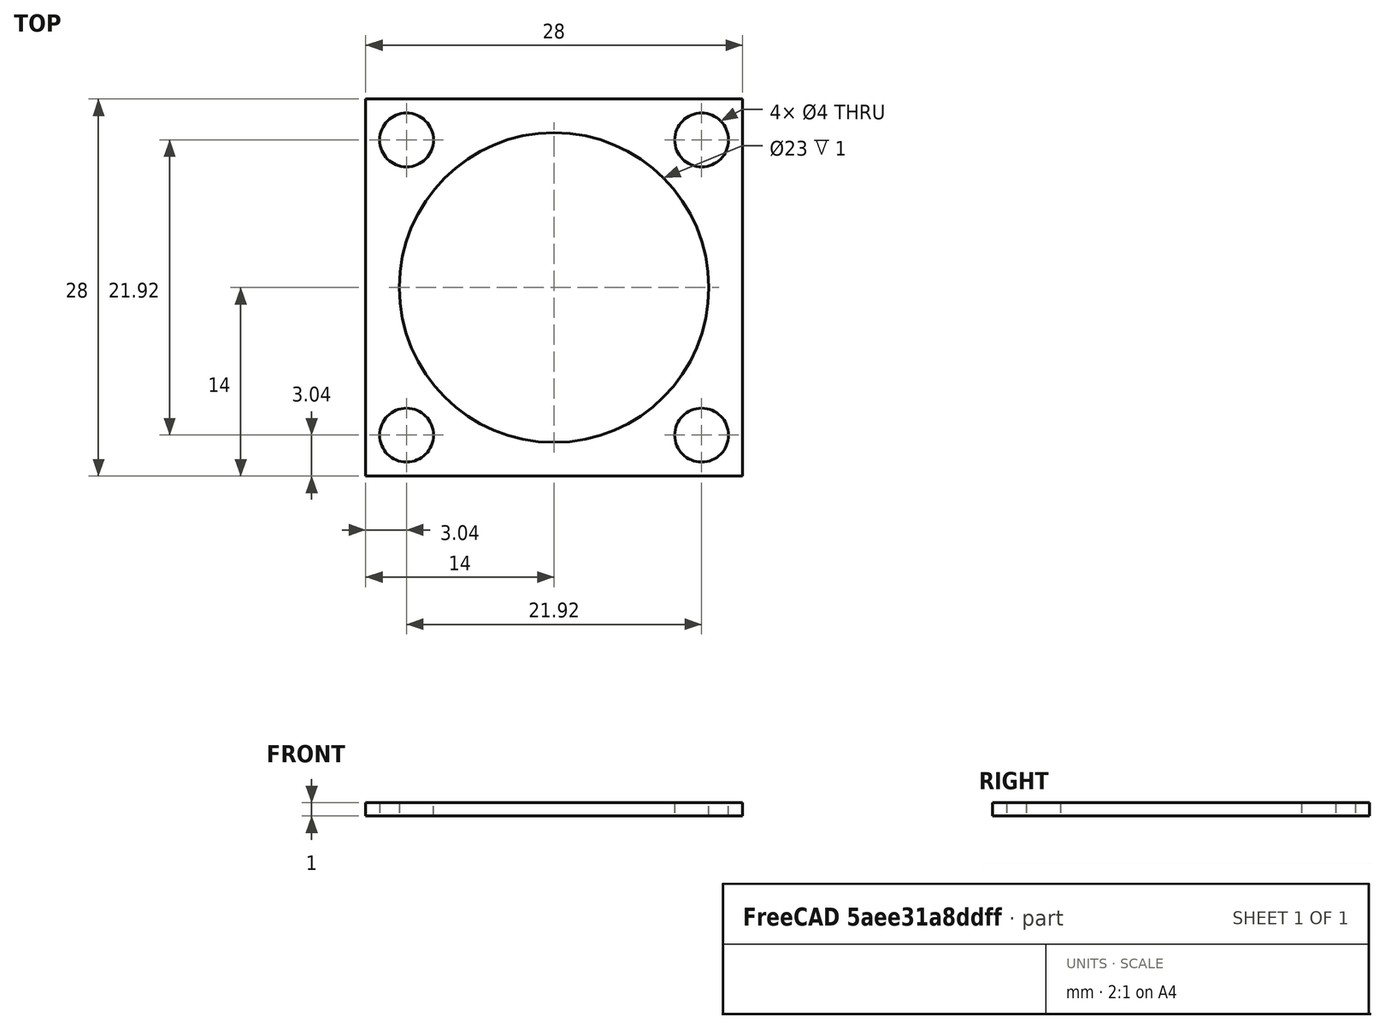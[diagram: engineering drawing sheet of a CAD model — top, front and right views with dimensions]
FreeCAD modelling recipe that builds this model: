
FCSTD DOCUMENT  (FreeCAD 0.19R24276 (Git))
Label: AS5048_holder_spacer
License: All rights reserved
LicenseURL: http://en.wikipedia.org/wiki/All_rights_reserved
objects: Sketcher::SketchObject×2, PartDesign::Body×2, PartDesign::Pad×1
note: 6 computed .brp shape members not serialized (recipe doc carries the construction recipe); baked Part::Feature solids carry a one-line shape summary decoded from their .brp

FEATURE [Sketcher::SketchObject] Sketch
  FullyConstrained = true
  MapMode = 5
  Support = -> [XY_Plane]
FEATURE [PartDesign::Body] Body
  Group = -> [Sketch]
  Origin = -> Origin
FEATURE [Sketcher::SketchObject] Sketch001
  FullyConstrained = false
  MapMode = 5
  Support = -> [XY_Plane001]
  sketch-geometry (9):
    g0: LineSegment StartX=-14 StartY=-14 StartZ=0 EndX=14 EndY=-14 EndZ=0
    g1: LineSegment StartX=14 StartY=-14 StartZ=0 EndX=14 EndY=14 EndZ=0
    g2: LineSegment StartX=14 StartY=14 StartZ=0 EndX=-14 EndY=14 EndZ=0
    g3: LineSegment StartX=-14 StartY=14 StartZ=0 EndX=-14 EndY=-14 EndZ=0
    g4: Circle CenterX=-10.9602 CenterY=10.9602 CenterZ=0 NormalX=0 NormalY=0 NormalZ=1 AngleXU=0 Radius=2
    g5: Circle CenterX=-10.9602 CenterY=-10.9602 CenterZ=0 NormalX=0 NormalY=0 NormalZ=1 AngleXU=0 Radius=2
    g6: Circle CenterX=10.9602 CenterY=10.9602 CenterZ=0 NormalX=0 NormalY=0 NormalZ=1 AngleXU=0 Radius=2
    g7: Circle CenterX=10.9602 CenterY=-10.9602 CenterZ=0 NormalX=0 NormalY=0 NormalZ=1 AngleXU=0 Radius=2
    g8: Circle CenterX=0 CenterY=0 CenterZ=0 NormalX=0 NormalY=0 NormalZ=1 AngleXU=0 Radius=11.5
  constraints (17):
    c: Coincident(g0,g1)
    c: Coincident(g1,g2)
    c: Coincident(g2,g3)
    c: Coincident(g3,g0)
    c: Horizontal(g0)
    c: Horizontal(g2)
    c: Vertical(g1)
    c: Vertical(g3)
    c: Distance(g1) = 28
    c: Distance(g2) = 28
    c: Symmetric(g2,g0,g-1)
    c: Diameter(g4) = 4
    c: Equal(g4,g5) = 4
    c: Equal(g4,g6) = 4
    c: Equal(g6,g7) = 4
    c: Coincident(g-1,g8)
    c: Diameter(g8) = 23
FEATURE [PartDesign::Pad] Pad
  Direction = (1,1,1)
  Length = 1
  Length2 = 100
  Profile = -> Sketch001
  Type = 0
FEATURE [PartDesign::Body] Body001
  Group = -> [Sketch001,Pad]
  Origin = -> Origin001
  Tip = -> Pad
